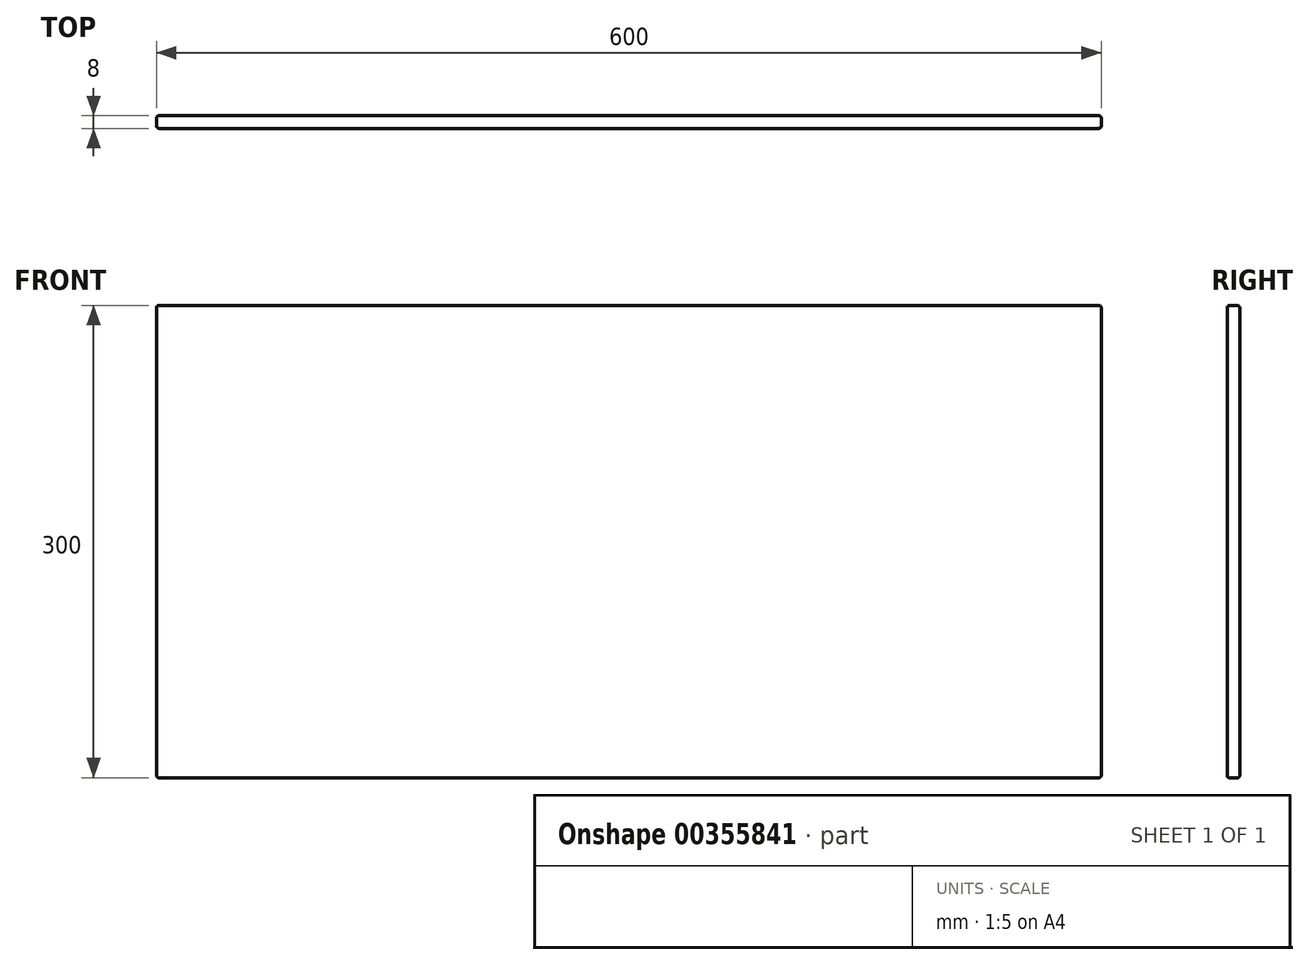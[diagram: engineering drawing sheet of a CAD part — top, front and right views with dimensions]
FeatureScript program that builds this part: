
annotation { "Feature Type Name" : "Feature", "Feature Type Description" : "" }
export const myFeature = defineFeature(function(context is Context, id is Id, definition is map)
    precondition{}
    {
        {
            var Q0;
            Q0=qCreatedBy(makeId("Front.planeOp"),FACE);
            var sketch = newSketch(context, id + "F0", { "sketchPlane" : qUnion([Q0])});
            skLineSegment(sketch, "E0.bottom", {"start": v(-303.63, 160.72) * mm, "end": v(296.37, 160.72) * mm});
            skLineSegment(sketch, "E0.top", {"start": v(-303.63, -139.28) * mm, "end": v(296.37, -139.28) * mm});
            skLineSegment(sketch, "E0.left", {"start": v(-303.63, 160.72) * mm, "end": v(-303.63, -139.28) * mm});
            skLineSegment(sketch, "E0.right", {"start": v(296.37, 160.72) * mm, "end": v(296.37, -139.28) * mm});
            skSolve(sketch);
        }
        {
            var Q0;
            Q0 = qSketchRegion(id + "F0", true);
            extrude(context, id + "F1", {"entities" : qUnion([Q0]), "depth" : 8 * mm});
        }
        {
            var Q0;
            Q0=makeQuery(id+"F1.opExtrude","SWEPT_FACE",FACE,{"disambiguationData":[OSD([sQuery(id+"F0.wireOp",EDGE,"E0.bottom")])]});
            var Q1;
            Q1=makeQuery(id+"F1.opExtrude","CAP_FACE",FACE,{"disambiguationData":[OSD([sQuery(id+"F0.wireOp",EDGE,"E0.bottom"),sQuery(id+"F0.wireOp",EDGE,"E0.top"),sQuery(id+"F0.wireOp",EDGE,"E0.left"),sQuery(id+"F0.wireOp",EDGE,"E0.right")])],"isStart":false});
            var Q2;
            Q2=makeQuery(id+"F1.opExtrude","SWEPT_FACE",FACE,{"disambiguationData":[OSD([sQuery(id+"F0.wireOp",EDGE,"E0.top")])]});
            var Q3;
            Q3=makeQuery(id+"F1.opExtrude","CAP_EDGE",EDGE,{"disambiguationData":[OSD([sQuery(id+"F0.wireOp",EDGE,"E0.bottom")])],"isStart":true});
            var Q4;
            Q4=makeQuery(id+"F1.opExtrude","SWEPT_FACE",FACE,{"disambiguationData":[OSD([sQuery(id+"F0.wireOp",EDGE,"E0.left")])]});
            var Q5;
            Q5=makeQuery(id+"F1.opExtrude","CAP_EDGE",EDGE,{"disambiguationData":[OSD([sQuery(id+"F0.wireOp",EDGE,"E0.bottom")])],"isStart":false});
            var Q6;
            Q6=makeQuery(id+"F1.opExtrude","SWEPT_FACE",FACE,{"disambiguationData":[OSD([sQuery(id+"F0.wireOp",EDGE,"E0.right")])]});
            var Q7;
            Q7=makeQuery(id+"F1.opExtrude","CAP_EDGE",EDGE,{"disambiguationData":[OSD([sQuery(id+"F0.wireOp",EDGE,"E0.top")])],"isStart":false});
            var Q8;
            Q8=makeQuery(id+"F1.opExtrude","SWEPT_EDGE",EDGE,{"disambiguationData":[OSD([sQuery(id+"F0.wireOp",EDGE,"E0.bottom"),sQuery(id+"F0.wireOp",EDGE,"E0.left")])]});
            var Q9;
            Q9=makeQuery(id+"F1.opExtrude","SWEPT_EDGE",EDGE,{"disambiguationData":[OSD([sQuery(id+"F0.wireOp",EDGE,"E0.bottom"),sQuery(id+"F0.wireOp",EDGE,"E0.right")])]});
            var Q10;
            Q10=makeQuery(id+"F1.opExtrude","CAP_FACE",FACE,{"disambiguationData":[OSD([sQuery(id+"F0.wireOp",EDGE,"E0.bottom"),sQuery(id+"F0.wireOp",EDGE,"E0.top"),sQuery(id+"F0.wireOp",EDGE,"E0.left"),sQuery(id+"F0.wireOp",EDGE,"E0.right")])],"isStart":true});
            var Q11;
            Q11=makeQuery(id+"F1.opExtrude","SWEPT_EDGE",EDGE,{"disambiguationData":[OSD([sQuery(id+"F0.wireOp",EDGE,"E0.top"),sQuery(id+"F0.wireOp",EDGE,"E0.left")])]});
            var Q12;
            Q12=makeQuery(id+"F1.opExtrude","SWEPT_EDGE",EDGE,{"disambiguationData":[OSD([sQuery(id+"F0.wireOp",EDGE,"E0.top"),sQuery(id+"F0.wireOp",EDGE,"E0.right")])]});
            var Q13;
            Q13=makeQuery(id+"F1.opExtrude","CAP_EDGE",EDGE,{"disambiguationData":[OSD([sQuery(id+"F0.wireOp",EDGE,"E0.top")])],"isStart":true});
            var Q14;
            Q14=makeQuery(id+"F1.opExtrude","CAP_EDGE",EDGE,{"disambiguationData":[OSD([sQuery(id+"F0.wireOp",EDGE,"E0.left")])],"isStart":false});
            var Q15;
            Q15=makeQuery(id+"F1.opExtrude","CAP_EDGE",EDGE,{"disambiguationData":[OSD([sQuery(id+"F0.wireOp",EDGE,"E0.right")])],"isStart":false});
            var Q16;
            Q16=makeQuery(id+"F1.opExtrude","CAP_EDGE",EDGE,{"disambiguationData":[OSD([sQuery(id+"F0.wireOp",EDGE,"E0.left")])],"isStart":true});
            var Q17;
            Q17=makeQuery(id+"F1.opExtrude","CAP_EDGE",EDGE,{"disambiguationData":[OSD([sQuery(id+"F0.wireOp",EDGE,"E0.right")])],"isStart":true});
            fillet(context, id + "F2", {"entities" : qUnion([Q0, Q1, Q2, Q3, Q4, Q5, Q6, Q7, Q8, Q9, Q10, Q11, Q12, Q13, Q14, Q15, Q16, Q17]), "radius" : 1.5 * mm, "tangentPropagation" : true, "allowEdgeOverflow" : false});
        }
    });
